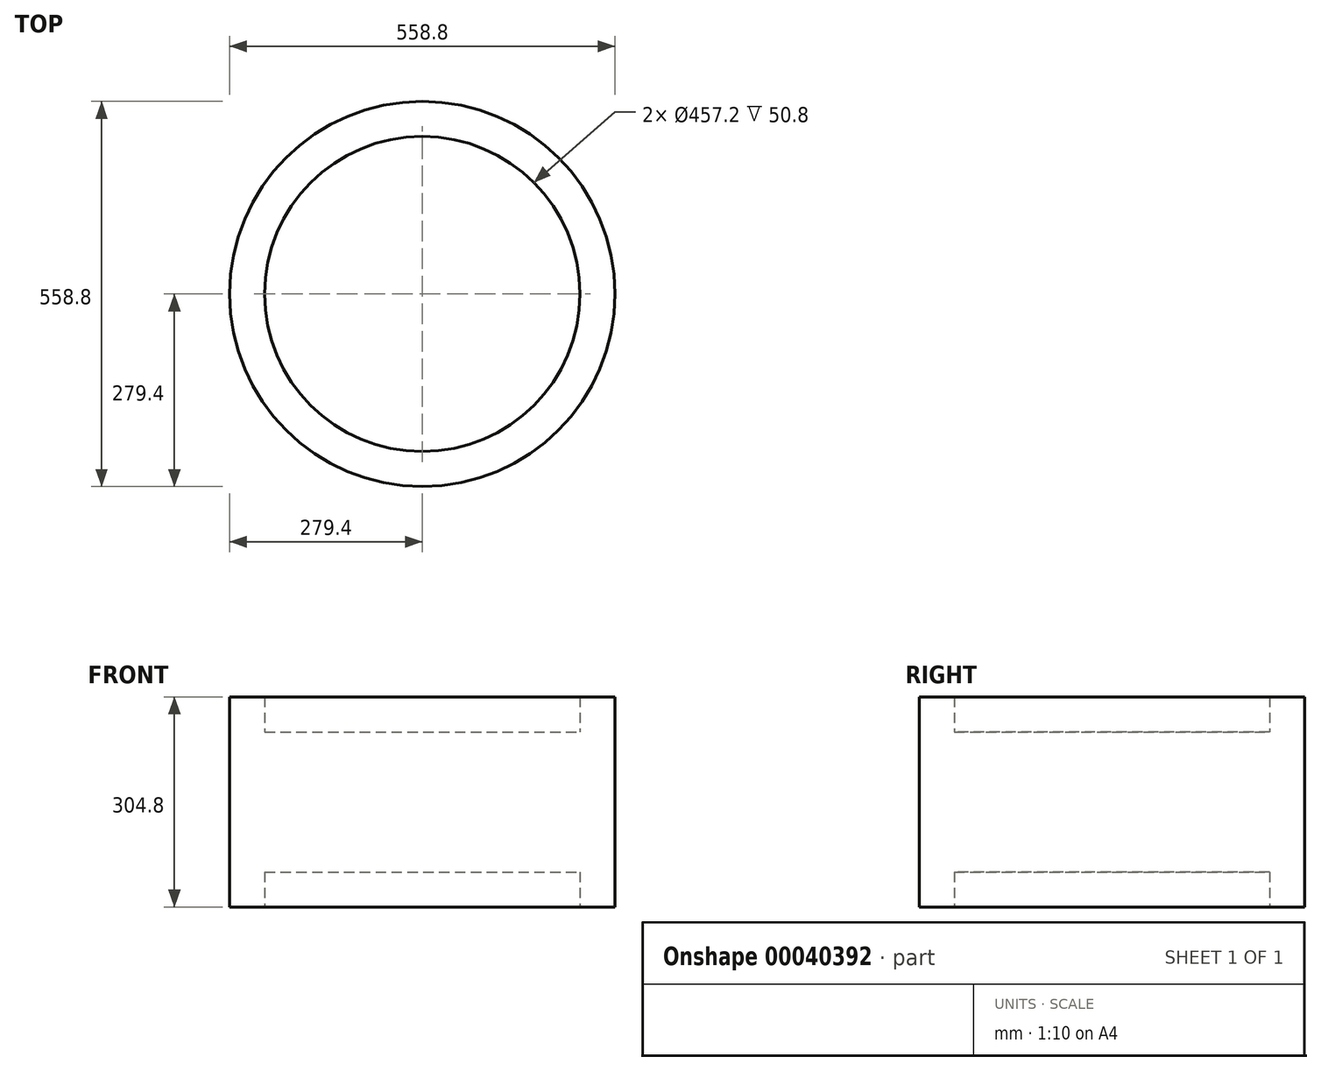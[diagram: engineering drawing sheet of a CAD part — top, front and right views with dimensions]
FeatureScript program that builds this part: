
annotation { "Feature Type Name" : "Feature", "Feature Type Description" : "" }
export const myFeature = defineFeature(function(context is Context, id is Id, definition is map)
    precondition{}
    {
        {
            var Q0;
            Q0=qCreatedBy(makeId("Right.planeOp"),FACE);
            var sketch = newSketch(context, id + "F0", { "sketchPlane" : qUnion([Q0])});
            skLineSegment(sketch, "E0.bottom", {"start": v(0, 0) * mm, "end": v(254, 0) * mm});
            skLineSegment(sketch, "E0.top", {"start": v(0, 203.2) * mm, "end": v(254, 203.2) * mm});
            skLineSegment(sketch, "E0.left", {"start": v(0, 0) * mm, "end": v(0, 203.2) * mm});
            skLineSegment(sketch, "E0.right", {"start": v(254, 0) * mm, "end": v(254, 203.2) * mm});
            skLineSegment(sketch, "E1.rect.bottom", {"start": v(279.4, 254) * mm, "end": v(228.6, 254) * mm});
            skLineSegment(sketch, "E1.rect.top", {"start": v(279.4, -50.8) * mm, "end": v(228.6, -50.8) * mm});
            skLineSegment(sketch, "E1.rect.left", {"start": v(279.4, 254) * mm, "end": v(279.4, -50.8) * mm});
            skLineSegment(sketch, "E1.rect.right", {"start": v(228.6, 254) * mm, "end": v(228.6, -50.8) * mm});
            skPoint(sketch, "E1.rect.middle", {"position": v(254, 101.6) * mm});
            skSolve(sketch);
        }
        {
            var Q0;
            Q0 = qSketchRegion(id + "F0", true);
            var Q1;
            Q1=sQuery(id+"F0.wireOp",EDGE,"E0.left");
            revolve(context, id + "F1", {"entities" : qUnion([Q0]), "axis" : qUnion([Q1]), "revolveType" : RevolveType.FULL});
        }
    });
